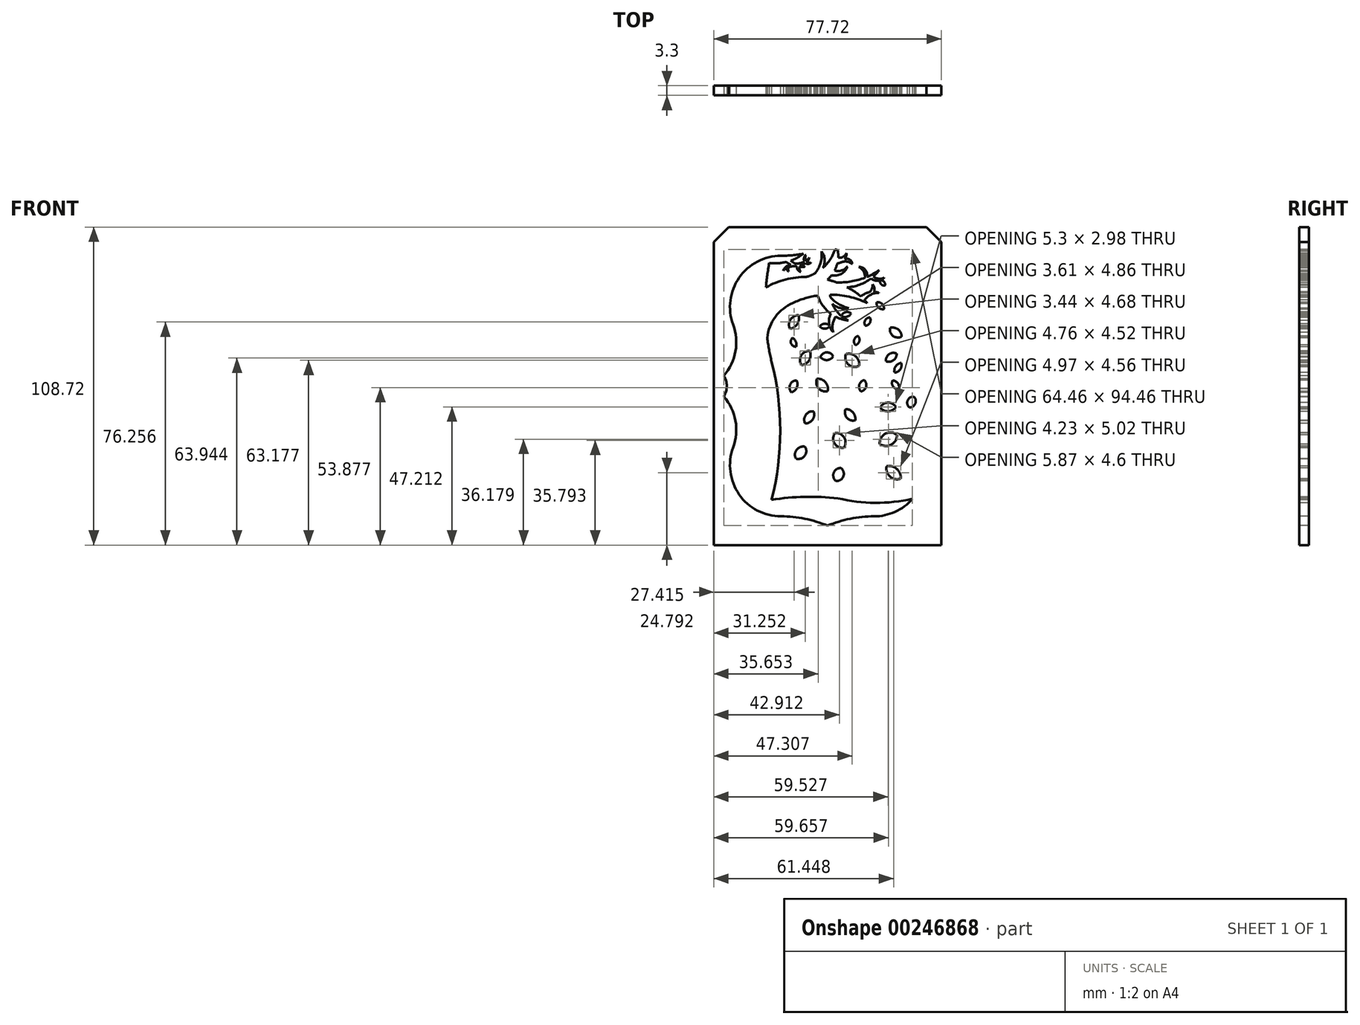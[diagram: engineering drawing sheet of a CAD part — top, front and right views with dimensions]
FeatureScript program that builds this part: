
annotation { "Feature Type Name" : "Feature", "Feature Type Description" : "" }
export const myFeature = defineFeature(function(context is Context, id is Id, definition is map)
    precondition{}
    {
        {
            var Q0;
            Q0=qCreatedBy(makeId("Front.planeOp"),FACE);
            var sketch = newSketch(context, id + "F0", { "sketchPlane" : qUnion([Q0])});
            skLineSegment(sketch, "E0.bottom", {"start": v(38.86, 54.36) * mm, "end": v(-38.86, 54.36) * mm});
            skLineSegment(sketch, "E0.top", {"start": v(38.86, -54.36) * mm, "end": v(-38.86, -54.36) * mm});
            skLineSegment(sketch, "E0.left", {"start": v(38.86, 54.36) * mm, "end": v(38.86, -54.36) * mm});
            skLineSegment(sketch, "E0.right", {"start": v(-38.86, 54.36) * mm, "end": v(-38.86, -54.36) * mm});
            skPoint(sketch, "E0.middle", {"position": v(0, 0) * mm});
            skSolve(sketch);
        }
        {
            var Q0;
            Q0=qSketchRegion(id+"F0",true);
            extrude(context, id + "F1", {"entities" : qUnion([Q0]), "depth" : 3.3 * mm});
        }
        {
            var Q0;
            Q0=makeQuery(id+"F1.opExtrude","CAP_FACE",FACE,{"disambiguationData":[OSD([sQuery(id+"F0.wireOp",EDGE,"E0.bottom"),sQuery(id+"F0.wireOp",EDGE,"E0.top"),sQuery(id+"F0.wireOp",EDGE,"E0.left"),sQuery(id+"F0.wireOp",EDGE,"E0.right")])],"isStart":false});
            var sketch = newSketch(context, id + "F2", { "sketchPlane" : qUnion([Q0])});
            skLineSegment(sketch, "E1", {"start": v(0, 57.24) * mm, "end": v(0, -57.24) * mm, "construction": true});
            skLineSegment(sketch, "E2", {"start": v(-50.8, 0) * mm, "end": v(50.8, 0) * mm, "construction": true});
            skArc(sketch, "E3", {"start": v(35.44, -3.57) * mm, "mid": v(31.46, -11.87) * mm, "end": v(32.26, -21.03) * mm});
            skLineSegment(sketch, "E4", {"start": v(15.88, -44.54) * mm, "end": v(0, -44.54) * mm, "construction": true});
            skArc(sketch, "E5", {"start": v(15.88, -44.54) * mm, "mid": v(30.2, -37.06) * mm, "end": v(32.26, -21.03) * mm});
            skArc(sketch, "E6", {"start": v(15.88, -44.54) * mm, "mid": v(7.78, -45.34) * mm, "end": v(0, -47.71) * mm});
            skArc(sketch, "E7.MirrorCS", {"start": v(-15.87, -44.54) * mm, "mid": v(-7.78, -45.34) * mm, "end": v(0, -47.71) * mm});
            skArc(sketch, "E8.MirrorCS", {"start": v(-15.87, -44.54) * mm, "mid": v(-30.2, -37.06) * mm, "end": v(-32.26, -21.03) * mm});
            skArc(sketch, "E9.MirrorCS", {"start": v(-35.44, -3.57) * mm, "mid": v(-31.46, -11.87) * mm, "end": v(-32.26, -21.03) * mm});
            skArc(sketch, "E10.MirrorCS", {"start": v(-35.44, 3.57) * mm, "mid": v(-31.46, 11.87) * mm, "end": v(-32.26, 21.03) * mm});
            skArc(sketch, "E11.MirrorCS", {"start": v(-15.88, 44.54) * mm, "mid": v(-30.2, 37.06) * mm, "end": v(-32.26, 21.03) * mm});
            skArc(sketch, "E12.MirrorCS", {"start": v(-15.88, 44.54) * mm, "mid": v(-7.78, 45.34) * mm, "end": v(0, 47.71) * mm});
            skArc(sketch, "E13.MirrorCS", {"start": v(15.87, 44.54) * mm, "mid": v(7.78, 45.34) * mm, "end": v(0, 47.71) * mm});
            skArc(sketch, "E14.MirrorCS", {"start": v(15.87, 44.54) * mm, "mid": v(30.2, 37.06) * mm, "end": v(32.26, 21.03) * mm});
            skArc(sketch, "E15.MirrorCS", {"start": v(35.44, 3.57) * mm, "mid": v(31.46, 11.87) * mm, "end": v(32.26, 21.03) * mm});
            skArc(sketch, "E16", {"start": v(35.44, 3.57) * mm, "mid": v(34.41, 0) * mm, "end": v(35.44, -3.57) * mm});
            skPoint(sketch, "E17.orphan", {"position": v(39.69, 0) * mm});
            skArc(sketch, "E18.MirrorCS", {"start": v(-35.44, 3.57) * mm, "mid": v(-34.41, 0) * mm, "end": v(-35.44, -3.57) * mm});
            skPoint(sketch, "E19.orphan", {"position": v(-39.69, 0) * mm});
            skSolve(sketch);
        }
        {
            var Q0;
            Q0=makeQuery(id+"F1.opExtrude","SWEPT_EDGE",EDGE,{"disambiguationData":[OSD([sQuery(id+"F0.wireOp",EDGE,"E0.bottom"),sQuery(id+"F0.wireOp",EDGE,"E0.right")])]});
            var Q1;
            Q1=makeQuery(id+"F1.opExtrude","SWEPT_EDGE",EDGE,{"disambiguationData":[OSD([sQuery(id+"F0.wireOp",EDGE,"E0.bottom"),sQuery(id+"F0.wireOp",EDGE,"E0.left")])]});
            chamfer(context, id + "F3", {"entities" : qUnion([Q0, Q1]), "width" : 5.08 * mm, "tangentPropagation" : true});
        }
        {
            var Q0;
            Q0=makeQuery(id+"F2.imprint","IMPRINT",FACE,{"disambiguationData":[TD([[makeQuery(id+"F2.imprint","IMPRINT",EDGE,{"derivedFrom":sQuery(id+"F2.wireOp",EDGE,"E3")}),-1.0]])]});
            var sketch = newSketch(context, id + "F4", { "sketchPlane" : qUnion([Q0])});
            skArc(sketch, "E20", {"start": v(3.54, -38.35) * mm, "mid": v(-7.8, -37.86) * mm, "end": v(-19.12, -38.87) * mm});
            skArc(sketch, "E21", {"start": v(3.54, -38.35) * mm, "mid": v(16.27, -39.9) * mm, "end": v(29.02, -38.57) * mm});
            skArc(sketch, "E22", {"start": v(-19.12, -38.87) * mm, "mid": v(-16.15, -15.26) * mm, "end": v(-19.12, 8.35) * mm});
            skArc(sketch, "E23", {"start": v(-11.74, 28.43) * mm, "mid": v(-17.82, 23.65) * mm, "end": v(-20.6, 16.43) * mm});
            skArc(sketch, "E24", {"start": v(13.5, 28.43) * mm, "mid": v(7.34, 30.55) * mm, "end": v(0.88, 31.26) * mm});
            skArc(sketch, "E25", {"start": v(13.5, 28.43) * mm, "mid": v(13.1, 28.9) * mm, "end": v(12.68, 29.37) * mm});
            skArc(sketch, "E26", {"start": v(2.96, 35.45) * mm, "mid": v(1.5, 35.96) * mm, "end": v(0, 36.4) * mm});
            skArc(sketch, "E27", {"start": v(6.63, 33.75) * mm, "mid": v(10.98, 34.65) * mm, "end": v(14.87, 36.8) * mm});
            skArc(sketch, "E28", {"start": v(2.96, 35.45) * mm, "mid": v(7.95, 35.75) * mm, "end": v(12.77, 37.06) * mm});
            skPoint(sketch, "E28.startSnap0", {"position": v(12.77, 35.45) * mm});
            skArc(sketch, "E29", {"start": v(-3.37, 30.96) * mm, "mid": v(-1.6, 27.49) * mm, "end": v(1.14, 24.74) * mm});
            skArc(sketch, "E30", {"start": v(0.88, 31.26) * mm, "mid": v(0.93, 30.8) * mm, "end": v(1, 30.35) * mm});
            skArc(sketch, "E31", {"start": v(-7.2, 37.31) * mm, "mid": v(-5.72, 37.81) * mm, "end": v(-4.31, 38.47) * mm});
            skArc(sketch, "E32", {"start": v(0, 36.4) * mm, "mid": v(0.74, 37.12) * mm, "end": v(1.4, 37.91) * mm});
            skArc(sketch, "E33", {"start": v(13.53, 37.37) * mm, "mid": v(12.87, 39.74) * mm, "end": v(10.62, 40.74) * mm});
            skPoint(sketch, "E33.endSnap0", {"position": v(10.62, 36.34) * mm});
            skArc(sketch, "E34", {"start": v(12.77, 37.06) * mm, "mid": v(12.3, 39.25) * mm, "end": v(10.62, 40.74) * mm});
            skArc(sketch, "E35", {"start": v(15.63, 37.44) * mm, "mid": v(17.43, 36.7) * mm, "end": v(19.35, 37) * mm});
            skArc(sketch, "E36", {"start": v(14.87, 36.8) * mm, "mid": v(16.36, 36.06) * mm, "end": v(18.03, 36.17) * mm});
            skArc(sketch, "E37", {"start": v(17.6, 31.9) * mm, "mid": v(16.78, 32.1) * mm, "end": v(15.95, 32.2) * mm});
            skArc(sketch, "E38", {"start": v(17.6, 31.9) * mm, "mid": v(14.82, 31.25) * mm, "end": v(12.68, 29.37) * mm});
            skArc(sketch, "E39", {"start": v(1.14, 24.74) * mm, "mid": v(0.5, 22.73) * mm, "end": v(0.67, 20.63) * mm});
            skArc(sketch, "E40", {"start": v(2.82, 23.7) * mm, "mid": v(1.73, 21.15) * mm, "end": v(1.97, 18.38) * mm});
            skArc(sketch, "E41", {"start": v(14.33, 32.08) * mm, "mid": v(15.18, 33.3) * mm, "end": v(15.4, 34.77) * mm});
            skArc(sketch, "E42", {"start": v(15.95, 32.2) * mm, "mid": v(16, 33.55) * mm, "end": v(15.4, 34.77) * mm});
            skArc(sketch, "E43", {"start": v(1.65, 28.14) * mm, "mid": v(4.24, 26.7) * mm, "end": v(7.21, 26.67) * mm});
            skArc(sketch, "E44", {"start": v(1, 30.35) * mm, "mid": v(3.82, 28.03) * mm, "end": v(7.21, 26.67) * mm});
            skArc(sketch, "E45", {"start": v(-1.61, 40.35) * mm, "mid": v(-0.98, 43.3) * mm, "end": v(-2.07, 46.1) * mm});
            skArc(sketch, "E46", {"start": v(-4.31, 38.47) * mm, "mid": v(-2.38, 42.05) * mm, "end": v(-2.07, 46.1) * mm});
            skArc(sketch, "E47", {"start": v(3.63, 43.86) * mm, "mid": v(5.33, 44.2) * mm, "end": v(6.52, 45.46) * mm});
            skArc(sketch, "E48", {"start": v(3.34, 41.94) * mm, "mid": v(3.95, 42.04) * mm, "end": v(4.53, 42.26) * mm});
            skArc(sketch, "E49", {"start": v(8.46, 41.73) * mm, "mid": v(7.59, 43.22) * mm, "end": v(5.87, 43.38) * mm});
            skArc(sketch, "E50", {"start": v(8.46, 41.73) * mm, "mid": v(6.53, 42.56) * mm, "end": v(4.46, 42.23) * mm});
            skArc(sketch, "E51", {"start": v(2.42, 39.5) * mm, "mid": v(4.84, 39.52) * mm, "end": v(6.82, 40.92) * mm});
            skArc(sketch, "E52", {"start": v(1.4, 37.91) * mm, "mid": v(4.7, 38.37) * mm, "end": v(6.82, 40.92) * mm});
            skArc(sketch, "E53", {"start": v(-19.9, 42.09) * mm, "mid": v(-17.02, 42) * mm, "end": v(-14.17, 42.41) * mm});
            skArc(sketch, "E54", {"start": v(-8.2, 45.26) * mm, "mid": v(-9.13, 44.66) * mm, "end": v(-10.04, 44.02) * mm});
            skArc(sketch, "E55", {"start": v(-14.17, 42.41) * mm, "mid": v(-13.33, 41.87) * mm, "end": v(-12.44, 41.43) * mm});
            skArc(sketch, "E56", {"start": v(-12.57, 42.88) * mm, "mid": v(-11.85, 42.33) * mm, "end": v(-11.08, 41.86) * mm});
            skArc(sketch, "E57", {"start": v(-10.44, 40.85) * mm, "mid": v(-10.15, 39.65) * mm, "end": v(-9.1, 39.01) * mm});
            skArc(sketch, "E58", {"start": v(-9.46, 40.74) * mm, "mid": v(-9.55, 39.82) * mm, "end": v(-9.1, 39.01) * mm});
            skArc(sketch, "E59", {"start": v(-11.08, 41.86) * mm, "mid": v(-9.44, 41.98) * mm, "end": v(-7.9, 42.55) * mm});
            skArc(sketch, "E60", {"start": v(-9.46, 41.18) * mm, "mid": v(-8.42, 41.43) * mm, "end": v(-7.5, 41.97) * mm});
            skArc(sketch, "E61", {"start": v(-6.97, 42.46) * mm, "mid": v(-6.36, 42.08) * mm, "end": v(-5.66, 42.21) * mm});
            skArc(sketch, "E62", {"start": v(-7.5, 41.97) * mm, "mid": v(-6.53, 41.75) * mm, "end": v(-5.66, 42.21) * mm});
            skArc(sketch, "E63", {"start": v(-7.37, 44.84) * mm, "mid": v(-8.05, 43.79) * mm, "end": v(-7.9, 42.55) * mm});
            skArc(sketch, "E64", {"start": v(-7.37, 44.84) * mm, "mid": v(-7.6, 43.85) * mm, "end": v(-7.37, 42.87) * mm});
            skArc(sketch, "E65", {"start": v(-12.44, 41.43) * mm, "mid": v(-14.1, 40.86) * mm, "end": v(-15.13, 39.43) * mm});
            skArc(sketch, "E66", {"start": v(-11.1, 40.99) * mm, "mid": v(-12.2, 40.91) * mm, "end": v(-13.27, 40.62) * mm});
            skArc(sketch, "E67", {"start": v(-13.6, 40.48) * mm, "mid": v(-13.82, 39.72) * mm, "end": v(-13.27, 39.14) * mm});
            skPoint(sketch, "E67.endSnap0", {"position": v(-13.27, 40.62) * mm});
            skArc(sketch, "E68", {"start": v(-13.27, 40.62) * mm, "mid": v(-13.44, 39.88) * mm, "end": v(-13.27, 39.14) * mm});
            skArc(sketch, "E69", {"start": v(0.67, 20.63) * mm, "mid": v(-1.07, 21.32) * mm, "end": v(-2.67, 20.36) * mm});
            skArc(sketch, "E70", {"start": v(-2.67, 20.36) * mm, "mid": v(-0.96, 19.6) * mm, "end": v(0.75, 20.36) * mm});
            skArc(sketch, "E71", {"start": v(8.04, 24.84) * mm, "mid": v(6.15, 25.25) * mm, "end": v(4.72, 23.96) * mm});
            skArc(sketch, "E72", {"start": v(18.03, 36.17) * mm, "mid": v(18.3, 34.78) * mm, "end": v(19.68, 34.44) * mm});
            skArc(sketch, "E73", {"start": v(19.68, 34.44) * mm, "mid": v(19.3, 35.65) * mm, "end": v(18.17, 36.22) * mm});
            skArc(sketch, "E74", {"start": v(4.89, 23.82) * mm, "mid": v(6.67, 23.7) * mm, "end": v(8.04, 24.84) * mm});
            skArc(sketch, "E75", {"start": v(16.76, 28.64) * mm, "mid": v(17.42, 26.84) * mm, "end": v(19.27, 26.32) * mm});
            skArc(sketch, "E76", {"start": v(19.27, 26.32) * mm, "mid": v(18.6, 28.12) * mm, "end": v(16.76, 28.64) * mm});
            skArc(sketch, "E77", {"start": v(14.47, 23.44) * mm, "mid": v(12.86, 22.48) * mm, "end": v(12.92, 20.6) * mm});
            skArc(sketch, "E78", {"start": v(12.92, 20.6) * mm, "mid": v(14.46, 21.6) * mm, "end": v(14.47, 23.44) * mm});
            skArc(sketch, "E79", {"start": v(-9.85, 24.24) * mm, "mid": v(-12.65, 22.73) * mm, "end": v(-12.86, 19.55) * mm});
            skArc(sketch, "E80", {"start": v(-12.86, 19.55) * mm, "mid": v(-10.32, 21.23) * mm, "end": v(-9.85, 24.24) * mm});
            skArc(sketch, "E81", {"start": v(21.34, 19.91) * mm, "mid": v(22.4, 17.15) * mm, "end": v(25.34, 16.9) * mm});
            skArc(sketch, "E82", {"start": v(25.34, 16.9) * mm, "mid": v(24.07, 19.38) * mm, "end": v(21.34, 19.91) * mm});
            skArc(sketch, "E83.trimOffspring", {"start": v(11.4, 30.63) * mm, "mid": v(9.13, 32.37) * mm, "end": v(6.63, 33.75) * mm});
            skArc(sketch, "E84.trimOffspring", {"start": v(14.33, 32.08) * mm, "mid": v(12.77, 31.54) * mm, "end": v(11.4, 30.63) * mm});
            skArc(sketch, "E85.trimOffspring", {"start": v(1.65, 28.14) * mm, "mid": v(2.93, 25.86) * mm, "end": v(4.72, 23.96) * mm});
            skArc(sketch, "E86.trimOffspring", {"start": v(-3.37, 30.96) * mm, "mid": v(-7.65, 30) * mm, "end": v(-11.74, 28.43) * mm});
            skArc(sketch, "E87.trimOffspring", {"start": v(2.82, 23.7) * mm, "mid": v(4.92, 22.87) * mm, "end": v(7.14, 22.42) * mm});
            skArc(sketch, "E88.trimOffspring", {"start": v(4.89, 23.82) * mm, "mid": v(5.97, 23.05) * mm, "end": v(7.14, 22.42) * mm});
            skArc(sketch, "E89.trimOffspring", {"start": v(0.75, 20.36) * mm, "mid": v(1.25, 19.3) * mm, "end": v(1.97, 18.38) * mm});
            skArc(sketch, "E90.trimOffspring", {"start": v(13.53, 37.37) * mm, "mid": v(15.63, 38.38) * mm, "end": v(17.62, 39.6) * mm});
            skArc(sketch, "E91.trimOffspring", {"start": v(15.63, 37.44) * mm, "mid": v(16.68, 38.46) * mm, "end": v(17.62, 39.6) * mm});
            skArc(sketch, "E92.trimOffspring", {"start": v(18.17, 36.22) * mm, "mid": v(18.8, 36.55) * mm, "end": v(19.35, 37) * mm});
            skArc(sketch, "E93.trimOffspring", {"start": v(2.42, 39.5) * mm, "mid": v(2.95, 40.69) * mm, "end": v(3.34, 41.94) * mm});
            skArc(sketch, "E94.trimOffspring", {"start": v(3.63, 43.86) * mm, "mid": v(3.64, 45.16) * mm, "end": v(3.5, 46.44) * mm});
            skArc(sketch, "E95.trimOffspring", {"start": v(5.87, 43.38) * mm, "mid": v(6.36, 44.36) * mm, "end": v(6.52, 45.46) * mm});
            skArc(sketch, "E96.trimOffspring", {"start": v(-1.61, 40.35) * mm, "mid": v(0.9, 43.27) * mm, "end": v(2.55, 46.75) * mm});
            skArc(sketch, "E97.trimOffspring", {"start": v(-7.2, 37.31) * mm, "mid": v(-14.34, 36.4) * mm, "end": v(-21.03, 33.75) * mm});
            skArc(sketch, "E98.trimOffspring", {"start": v(-20.6, 16.43) * mm, "mid": v(-19.97, 12.37) * mm, "end": v(-19.12, 8.35) * mm});
            skArc(sketch, "E99.trimOffspring", {"start": v(-11.1, 40.99) * mm, "mid": v(-10.77, 40.91) * mm, "end": v(-10.44, 40.85) * mm});
            skArc(sketch, "E100.trimOffspring", {"start": v(-13.6, 40.48) * mm, "mid": v(-14.4, 40.02) * mm, "end": v(-15.13, 39.43) * mm});
            skArc(sketch, "E101.trimOffspring", {"start": v(-9.46, 40.74) * mm, "mid": v(-8.58, 40.74) * mm, "end": v(-7.7, 40.82) * mm});
            skArc(sketch, "E102.trimOffspring", {"start": v(-9.46, 41.18) * mm, "mid": v(-8.6, 40.96) * mm, "end": v(-7.7, 40.82) * mm});
            skArc(sketch, "E103.trimOffspring", {"start": v(-6.97, 42.46) * mm, "mid": v(-6.5, 43.15) * mm, "end": v(-6.18, 43.93) * mm});
            skArc(sketch, "E104.trimOffspring", {"start": v(-7.37, 42.87) * mm, "mid": v(-6.74, 43.36) * mm, "end": v(-6.18, 43.93) * mm});
            skArc(sketch, "E105.trimOffspring", {"start": v(-12.57, 42.88) * mm, "mid": v(-11.28, 43.4) * mm, "end": v(-10.04, 44.02) * mm});
            skArc(sketch, "E106.0", {"start": v(15.88, -44.54) * mm, "mid": v(23.1, -42.98) * mm, "end": v(29.02, -38.57) * mm});
            skArc(sketch, "E107.0", {"start": v(15.88, -44.54) * mm, "mid": v(7.78, -45.34) * mm, "end": v(0, -47.71) * mm});
            skArc(sketch, "E108.0", {"start": v(-15.87, -44.54) * mm, "mid": v(-7.78, -45.34) * mm, "end": v(0, -47.71) * mm});
            skArc(sketch, "E109.0", {"start": v(-15.87, -44.54) * mm, "mid": v(-30.2, -37.06) * mm, "end": v(-32.26, -21.03) * mm});
            skArc(sketch, "E110.0", {"start": v(-35.44, -3.57) * mm, "mid": v(-31.46, -11.87) * mm, "end": v(-32.26, -21.03) * mm});
            skArc(sketch, "E111.0", {"start": v(-35.44, 3.57) * mm, "mid": v(-34.41, 0) * mm, "end": v(-35.44, -3.57) * mm});
            skArc(sketch, "E112.0", {"start": v(-35.44, 3.57) * mm, "mid": v(-31.46, 11.87) * mm, "end": v(-32.26, 21.03) * mm});
            skArc(sketch, "E113.0", {"start": v(-15.88, 44.54) * mm, "mid": v(-30.2, 37.06) * mm, "end": v(-32.26, 21.03) * mm});
            skArc(sketch, "E114.0", {"start": v(-15.88, 44.54) * mm, "mid": v(-12.02, 44.72) * mm, "end": v(-8.2, 45.26) * mm});
            skArc(sketch, "E115.0", {"start": v(3.5, 46.44) * mm, "mid": v(3.02, 46.6) * mm, "end": v(2.55, 46.75) * mm});
            skArc(sketch, "E116.trimOffspring", {"start": v(-19.9, 42.09) * mm, "mid": v(-20.57, 37.94) * mm, "end": v(-21.03, 33.75) * mm});
            skPoint(sketch, "E117.start.orphan", {"position": v(-19.12, 45.77) * mm});
            skPoint(sketch, "E118.orphan", {"position": v(0, 47.71) * mm});
            skPoint(sketch, "E119.orphan", {"position": v(2.96, 48.4) * mm});
            skPoint(sketch, "E120.orphan", {"position": v(15.87, 44.54) * mm});
            skPoint(sketch, "E121.orphan", {"position": v(32.26, -21.03) * mm});
            skPoint(sketch, "E122.orphan", {"position": v(29.98, -38.35) * mm});
            skArc(sketch, "E123", {"start": v(-6.09, 12.01) * mm, "mid": v(-8.99, 10.45) * mm, "end": v(-8.9, 7.16) * mm});
            skArc(sketch, "E124", {"start": v(-8.9, 7.16) * mm, "mid": v(-6.27, 8.87) * mm, "end": v(-6.09, 12.01) * mm});
            skArc(sketch, "E125", {"start": v(6.3, 10.96) * mm, "mid": v(7.13, 7.35) * mm, "end": v(10.8, 6.94) * mm});
            skArc(sketch, "E126", {"start": v(10.8, 6.94) * mm, "mid": v(9.63, 10.16) * mm, "end": v(6.3, 10.96) * mm});
            skArc(sketch, "E127", {"start": v(23.64, 11.09) * mm, "mid": v(21, 10.88) * mm, "end": v(19.98, 8.45) * mm});
            skArc(sketch, "E128", {"start": v(19.98, 8.45) * mm, "mid": v(22.5, 8.82) * mm, "end": v(23.64, 11.09) * mm});
            skArc(sketch, "E129", {"start": v(10.43, 17.1) * mm, "mid": v(9.1, 15.82) * mm, "end": v(9.54, 14.04) * mm});
            skArc(sketch, "E130", {"start": v(9.54, 14.04) * mm, "mid": v(10.86, 15.31) * mm, "end": v(10.43, 17.1) * mm});
            skArc(sketch, "E131", {"start": v(-12.06, 16.41) * mm, "mid": v(-12.41, 14.5) * mm, "end": v(-10.76, 13.47) * mm});
            skArc(sketch, "E132", {"start": v(-10.76, 13.47) * mm, "mid": v(-10.84, 15.2) * mm, "end": v(-12.06, 16.41) * mm});
            skArc(sketch, "E133", {"start": v(-3.64, 2.46) * mm, "mid": v(-3.1, -0.76) * mm, "end": v(0, -1.78) * mm});
            skArc(sketch, "E134", {"start": v(0, -1.78) * mm, "mid": v(-0.7, 1.3) * mm, "end": v(-3.64, 2.46) * mm});
            skArc(sketch, "E135", {"start": v(12.53, 2.05) * mm, "mid": v(10.87, 0.4) * mm, "end": v(11.4, -1.87) * mm});
            skArc(sketch, "E136", {"start": v(11.4, -1.87) * mm, "mid": v(13.16, -0.26) * mm, "end": v(12.53, 2.05) * mm});
            skArc(sketch, "E137", {"start": v(22.26, 1.96) * mm, "mid": v(22.43, -0.21) * mm, "end": v(24.5, -0.86) * mm});
            skArc(sketch, "E138", {"start": v(24.5, -0.86) * mm, "mid": v(23.96, 1) * mm, "end": v(22.26, 1.96) * mm});
            skArc(sketch, "E139", {"start": v(-4.74, -8.64) * mm, "mid": v(-7.44, -9.83) * mm, "end": v(-7.65, -12.77) * mm});
            skArc(sketch, "E140", {"start": v(-7.65, -12.77) * mm, "mid": v(-5.1, -11.48) * mm, "end": v(-4.74, -8.64) * mm});
            skArc(sketch, "E141", {"start": v(23.32, -7.15) * mm, "mid": v(20.59, -5.66) * mm, "end": v(18.02, -7.4) * mm});
            skArc(sketch, "E142", {"start": v(18.02, -7.4) * mm, "mid": v(20.73, -8.64) * mm, "end": v(23.32, -7.15) * mm});
            skArc(sketch, "E143", {"start": v(6.17, -7.89) * mm, "mid": v(6.6, -10.84) * mm, "end": v(9.47, -11.7) * mm});
            skArc(sketch, "E144", {"start": v(9.47, -11.7) * mm, "mid": v(8.72, -9.02) * mm, "end": v(6.17, -7.89) * mm});
            skArc(sketch, "E145", {"start": v(-10.57, 1.93) * mm, "mid": v(-12.78, 0.45) * mm, "end": v(-12.34, -2.17) * mm});
            skArc(sketch, "E146", {"start": v(-12.34, -2.17) * mm, "mid": v(-10.53, -0.52) * mm, "end": v(-10.57, 1.93) * mm});
            skArc(sketch, "E147", {"start": v(1.9, 10.13) * mm, "mid": v(-0.34, 11.52) * mm, "end": v(-2.4, 9.86) * mm});
            skArc(sketch, "E148", {"start": v(-2.4, 9.86) * mm, "mid": v(-0.18, 8.88) * mm, "end": v(1.9, 10.13) * mm});
            skArc(sketch, "E149", {"start": v(29.59, -3.68) * mm, "mid": v(27.38, -4.88) * mm, "end": v(28, -7.3) * mm});
            skArc(sketch, "E150", {"start": v(28, -7.3) * mm, "mid": v(29.98, -6.02) * mm, "end": v(29.59, -3.68) * mm});
            skArc(sketch, "E151", {"start": v(25.13, 7.95) * mm, "mid": v(23.3, 6.76) * mm, "end": v(22.85, 4.62) * mm});
            skArc(sketch, "E152", {"start": v(22.85, 4.62) * mm, "mid": v(24.84, 5.7) * mm, "end": v(25.13, 7.95) * mm});
            skArc(sketch, "E153", {"start": v(23.73, -16.7) * mm, "mid": v(19.74, -16.28) * mm, "end": v(17.86, -19.83) * mm});
            skArc(sketch, "E154", {"start": v(17.86, -19.83) * mm, "mid": v(21.75, -20.04) * mm, "end": v(23.73, -16.7) * mm});
            skArc(sketch, "E155", {"start": v(2.6, -16.06) * mm, "mid": v(2.4, -19.6) * mm, "end": v(5.65, -21.04) * mm});
            skArc(sketch, "E156", {"start": v(5.65, -21.04) * mm, "mid": v(5.69, -17.59) * mm, "end": v(2.6, -16.06) * mm});
            skArc(sketch, "E157", {"start": v(-7.7, -20.74) * mm, "mid": v(-10.57, -21.76) * mm, "end": v(-10.82, -24.79) * mm});
            skArc(sketch, "E158", {"start": v(-10.82, -24.79) * mm, "mid": v(-7.81, -23.88) * mm, "end": v(-7.7, -20.74) * mm});
            skArc(sketch, "E159", {"start": v(20.2, -27.34) * mm, "mid": v(21.35, -30.94) * mm, "end": v(25.07, -31.64) * mm});
            skArc(sketch, "E160", {"start": v(25.07, -31.64) * mm, "mid": v(23.66, -28.32) * mm, "end": v(20.2, -27.34) * mm});
            skArc(sketch, "E161", {"start": v(4.6, -28.03) * mm, "mid": v(2.13, -29.6) * mm, "end": v(2.86, -32.43) * mm});
            skArc(sketch, "E162", {"start": v(2.86, -32.43) * mm, "mid": v(5.4, -30.9) * mm, "end": v(4.6, -28.03) * mm});
            skSolve(sketch);
        }
        {
            var Q0;
            Q0 = qSketchRegion(id + "F4", true);
            extrude(context, id + "F5", {"entities" : qUnion([Q0]), "operationType" : NewBodyOperationType.REMOVE, "endBound" : BoundingType.THROUGH_ALL, "oppositeDirection" : true, "depth" : 25.4 * mm});
        }
    });
